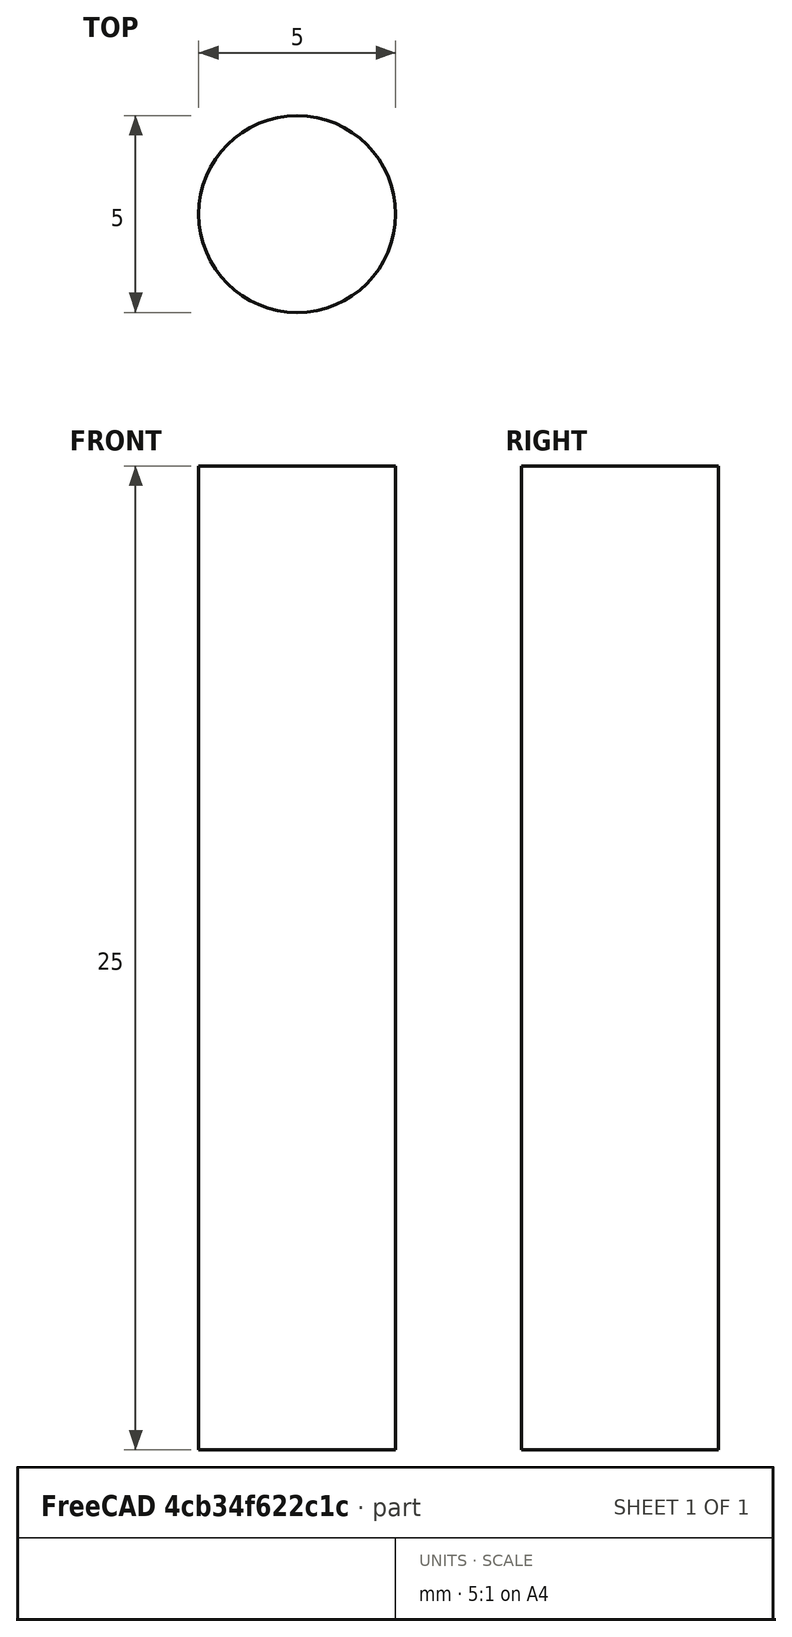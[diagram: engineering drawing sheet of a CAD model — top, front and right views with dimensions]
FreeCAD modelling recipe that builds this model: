
FCSTD DOCUMENT  (FreeCAD 1.0R39319 (Git))
Label: Airpods
License: All rights reserved
LicenseURL: https://en.wikipedia.org/wiki/All_rights_reserved
objects: Part::FeaturePython×7, Sketcher::SketchObject×5, Part::Part2DObjectPython×2, Part::Loft×2, Part::Extrusion×2, Part::MultiFuse×2, Part::Mirroring×1, Part::Revolution×1, PartDesign::SubShapeBinder×1, Part::RuledSurface×1, App::DocumentObjectGroup×1
note: 29 computed .brp shape members not serialized (recipe doc carries the construction recipe); baked Part::Feature solids carry a one-line shape summary decoded from their .brp

FEATURE [Sketcher::SketchObject] Sketch  label="Front_Profile"
  ArcFitTolerance = 1e-06
  FullyConstrained = true
  MakeInternals = false
  Placement = pos=(0,0,0) rot=(1,0,0;1.5708rad)
  sketch-geometry (9):
    g0-g4: Circle [constr] x5 (B-spline internal-alignment scaffolding for g5; pole/knot coordinates omitted)
    g5: BSplineCurve PolesCount=5 KnotsCount=3 Degree=3 IsPeriodic=0
    g6: GeomPoint [constr] X=-2 Y=0 Z=0
    g7: GeomPoint [constr] X=0 Y=3.5 Z=0
    g8: GeomPoint [constr] X=2 Y=0 Z=0
  constraints (15):
    c: Weight(g0) = 1
    c: Equal(g0, g1-g4) x4
    c: InternalAlignment(g0-g4 -> g5) x5
    c: InternalAlignment(g6,g5)
    c: InternalAlignment(g7,g5)
    c: InternalAlignment(g8,g5)
    c: PointOnObject(g0,g-1)
    c: PointOnObject(g2,g-2)
    c: PointOnObject(g4,g-1)
    c: Coincident(g7,g2)
    c: Vertical(g1,g5)
    c: Vertical(g3,g5)
    c: Horizontal(g1,g3)
    c: DistanceX(g1,g3) = 4
    c: DistanceY(g-1,g3) = 3.5
FEATURE [Sketcher::SketchObject] Sketch001  label="Mid_profile"
  ArcFitTolerance = 1e-06
  FullyConstrained = true
  MakeInternals = false
  Placement = pos=(0,8,0) rot=(1,0,0;1.5708rad)
  sketch-geometry (5):
    g0: ArcOfEllipse CenterX=0 CenterY=0 CenterZ=0 NormalX=0 NormalY=0 NormalZ=1 MajorRadius=7.5 MinorRadius=5 AngleXU=1.5708 StartAngle=4.71239 EndAngle=7.85398
    g1: LineSegment [constr] StartX=0 StartY=7.5 StartZ=0 EndX=0 EndY=-7.5 EndZ=0
    g2: LineSegment [constr] StartX=-5 StartY=0 StartZ=0 EndX=5 EndY=0 EndZ=0
    g3: GeomPoint [constr] X=0 Y=5.59017 Z=0
    g4: GeomPoint [constr] X=0 Y=-5.59017 Z=0
  constraints (7):
    c: InternalAlignment(g1-g4 -> g0) x4
    c: Coincident(g0,g-1)
    c: PointOnObject(g0,g2)
    c: Horizontal(g2)
    c: DistanceX(g0,g0) = 10
    c: DistanceY(g-1,g1) = 7.5
    c: PointOnObject(g0,g-1)
FEATURE [Part::Part2DObjectPython] Clone2D  label="End_profile"  # Draft 2D object (typed FeaturePython)
  Fuse = false
  Objects = -> [Sketch001]
  Placement = pos=(0,10,0) rot=(1,0,0;1.5708rad)
  Scale = (1,1,1)
FEATURE [Part::Loft] Loft
  Closed = false
  MaxDegree = 5
  Ruled = false
  Sections = -> [Sketch,Sketch001,Clone2D]
  Solid = false
FEATURE [Part::Mirroring] Part__Mirroring  label="Loft (Mirror #1)"
  Base = (0,0,0)
  Normal = (0,0,1)
  Source = -> Loft
FEATURE [Sketcher::SketchObject] Sketch002  label="Ref_Revolve_Axis"
  ArcFitTolerance = 1e-06
  ExternalGeometry = -> [Part__Mirroring]
  FullyConstrained = true
  MakeInternals = false
  sketch-geometry (1):
    g0: LineSegment StartX=-5 StartY=10 StartZ=0 EndX=5 EndY=10 EndZ=0
  constraints (2):
    c: Coincident(g0,g-3)
    c: Coincident(g0,g-3)
FEATURE [Part::Revolution] Revolve
  Angle = -180
  Axis = (1,0,0)
  AxisLink = -> Sketch002 [Edge1]
  Base = (5,10,0)
  FaceMakerClass = Part::FaceMakerBullseye
  Solid = false
  Source = -> Clone2D
  Symmetric = false
FEATURE [Sketcher::SketchObject] Sketch003
  ArcFitTolerance = 1e-06
  FullyConstrained = false
  MakeInternals = false
  sketch-geometry (11):
    g0-g5: Circle [constr] x6 (B-spline internal-alignment scaffolding for g6; pole/knot coordinates omitted)
    g6: BSplineCurve PolesCount=6 KnotsCount=4 Degree=3 IsPeriodic=0
    g7-g10: GeomPoint [constr] x4 (B-spline internal-alignment scaffolding for g6; pole/knot coordinates omitted)
  constraints (5):
    c: Weight(g0) = 1
    c: Equal(g0, g1-g5) x5
    c: InternalAlignment(g0-g5 -> g6) x6
    c: InternalAlignment(g7-g10 -> g6) x4
    c: PointOnObject(g5,g-1)
FEATURE [Part::Extrusion] Extrude
  Base = -> Sketch003
  Dir = (0,0,1)
  DirMode = 2
  FaceMakerClass = Part::FaceMakerBullseye
  FaceMakerMode = 3
  LengthFwd = 20
  LengthRev = 0
  Solid = false
  Symmetric = true
FEATURE [Part::MultiFuse] Fusion
  Refine = true
  Shapes = -> [Part__Mirroring,Loft,Revolve]
FEATURE [Part::FeaturePython] Slice  # WARN: FeaturePython — macro-defined, semantics opaque (R4)
  Base = -> Fusion
  Mode = 1
  Tolerance = 0
  Tools = -> [Extrude]
FEATURE [Part::FeaturePython] Slice_child0  label="Slice.0"  # WARN: FeaturePython — macro-defined, semantics opaque (R4)
  Base = -> Slice
  FilterType = 1
  Invert = false
  OverrideMaxVal = 0
  WindowFrom = 80
  WindowTo = 100
  items = 0
FEATURE [Part::FeaturePython] Slice_child1  label="Slice.1"  # WARN: FeaturePython — macro-defined, semantics opaque (R4)
  Base = -> Slice
  FilterType = 1
  Invert = false
  OverrideMaxVal = 0
  WindowFrom = 80
  WindowTo = 100
  items = 1
FEATURE [Part::FeaturePython] Slice_child2  label="Slice.2"  # WARN: FeaturePython — macro-defined, semantics opaque (R4)
  Base = -> Slice
  FilterType = 1
  Invert = false
  OverrideMaxVal = 0
  WindowFrom = 80
  WindowTo = 100
  items = 2
FEATURE [Part::FeaturePython] Slice_child3  label="Slice.3"  # WARN: FeaturePython — macro-defined, semantics opaque (R4)
  Base = -> Slice
  FilterType = 1
  Invert = false
  OverrideMaxVal = 0
  WindowFrom = 80
  WindowTo = 100
  items = 3
FEATURE [Part::FeaturePython] Slice_child4  label="Slice.4"  # WARN: FeaturePython — macro-defined, semantics opaque (R4)
  Base = -> Slice
  FilterType = 1
  Invert = false
  OverrideMaxVal = 0
  WindowFrom = 80
  WindowTo = 100
  items = 4
FEATURE [Part::FeaturePython] Slice_child5  label="Slice.5"  # WARN: FeaturePython — macro-defined, semantics opaque (R4)
  Base = -> Slice
  FilterType = 1
  Invert = false
  OverrideMaxVal = 0
  WindowFrom = 80
  WindowTo = 100
  items = 5
FEATURE [Sketcher::SketchObject] Sketch004  label="Stem_Profile"
  ArcFitTolerance = 1e-06
  FullyConstrained = true
  MakeInternals = false
  Placement = pos=(0,0,-5) rot=(0,0,1;0rad)
  sketch-geometry (1):
    g0: Circle CenterX=10 CenterY=12 CenterZ=0 NormalX=0 NormalY=0 NormalZ=1 AngleXU=0 Radius=2.5
  constraints (3):
    c: Diameter(g0) = 5
    c: DistanceY(g-1,g0) = 12
    c: DistanceX(g-1,g0) = 10
FEATURE [Part::Extrusion] Extrude001  label="Stem_Extrud"
  Base = -> Sketch004
  Dir = (0,0,1)
  DirMode = 2
  FaceMakerClass = Part::FaceMakerBullseye
  FaceMakerMode = 3
  LengthFwd = -25
  LengthRev = 0
  Solid = true
  Symmetric = false
FEATURE [Part::Part2DObjectPython] Clone2D001  label="Stem_Profile (2D)"  # Draft 2D object (typed FeaturePython)
  Fuse = false
  Objects = -> [Sketch004]
  Placement = pos=(-0.189469,0,-5.1566) rot=(0,1,0;6.02139rad)
  Scale = (1,1,1)
FEATURE [PartDesign::SubShapeBinder] Binder
  BindCopyOnChange = 0
  BindMode = 0
  ClaimChildren = false
  Fuse = false
  MakeFace = true
  OffsetFill = false
  OffsetIntersection = false
  OffsetJoinType = 0
  OffsetOpenResult = false
  PartialLoad = false
  Refine = true
  Relative = true
  Support = -> [Slice_child0[Edge3],Slice_child2[Edge3],Slice_child5[Edge4]]
  _Version = 2
FEATURE [Part::Loft] Loft001
  Closed = false
  MaxDegree = 5
  Ruled = false
  Sections = -> [Binder,Clone2D001,Sketch004]
  Solid = false
FEATURE [Part::RuledSurface] Ruled_Surface
  Curve1 = -> Slice_child2 [Edge5]
  Curve2 = -> Slice_child0 [Edge5]
  Orientation = 0
FEATURE [Part::MultiFuse] Fusion001
  Refine = true
  Shapes = -> [Slice_child2,Ruled_Surface,Slice_child5,Loft001,Slice_child0]
FEATURE [App::DocumentObjectGroup] GrExplode_Slice  label="Exploded Slice"
  Group = -> [Slice_child1,Slice_child3,Slice_child4,Fusion001]
